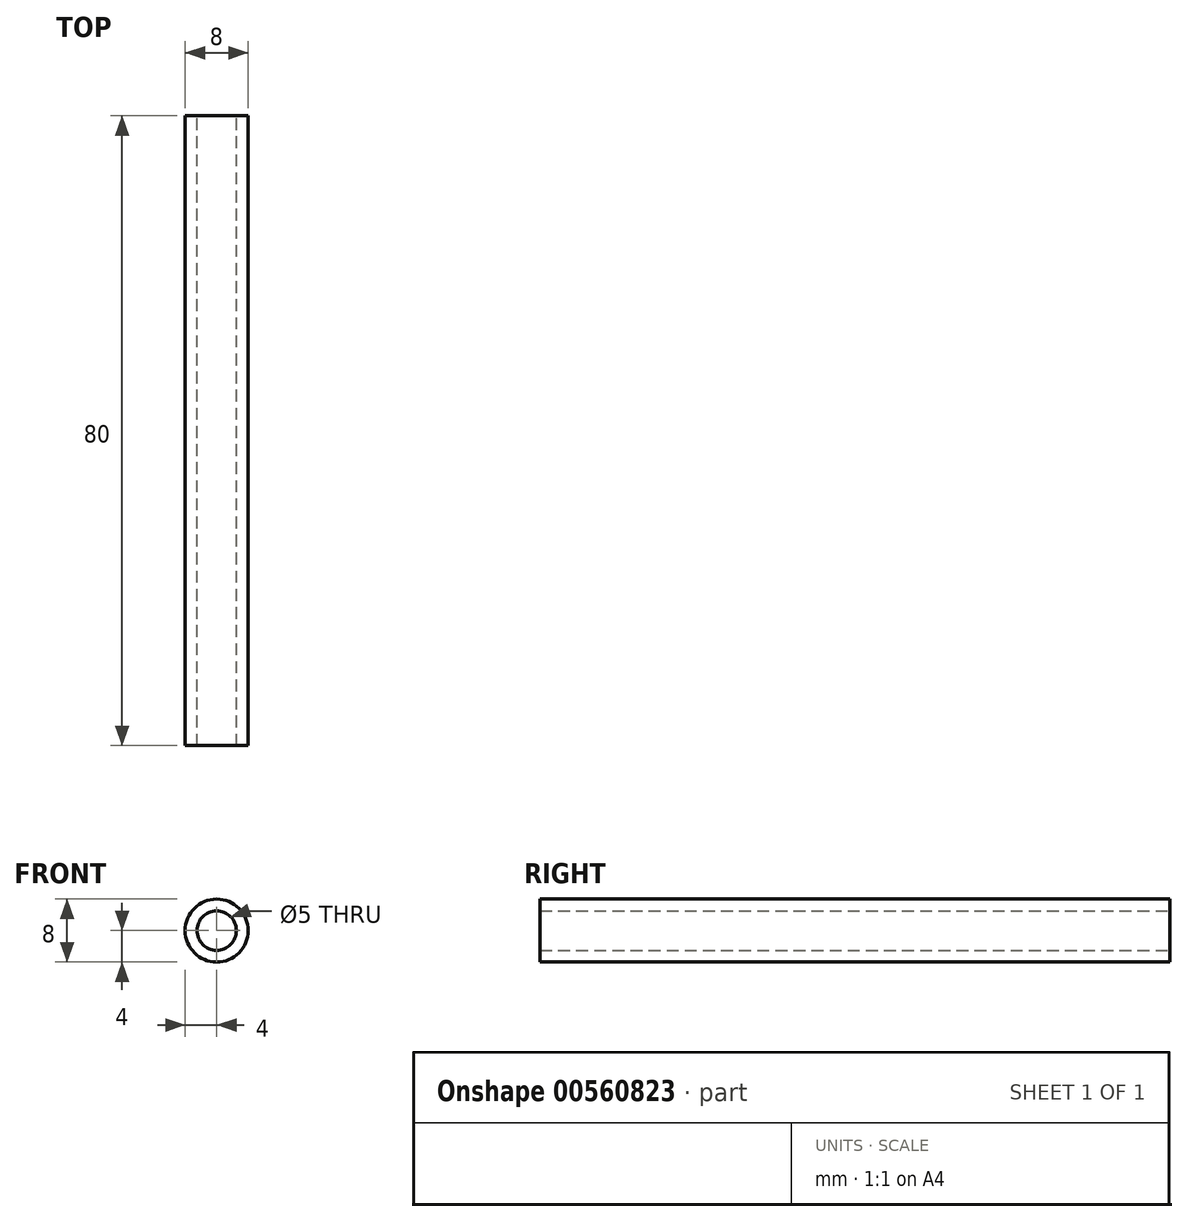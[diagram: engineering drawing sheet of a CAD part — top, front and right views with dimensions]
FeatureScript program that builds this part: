
annotation { "Feature Type Name" : "Feature", "Feature Type Description" : "" }
export const myFeature = defineFeature(function(context is Context, id is Id, definition is map)
    precondition{}
    {
        {
            var Q0;
            Q0=qCreatedBy(makeId("Front.planeOp"),FACE);
            var sketch = newSketch(context, id + "F0", { "sketchPlane" : qUnion([Q0])});
            skCircle(sketch, "E0", {"center": v(0, 0) * mm, "radius": 4 * mm});
            skCircle(sketch, "E1", {"center": v(0, 0) * mm, "radius": 2.5 * mm});
            skSolve(sketch);
        }
        {
            var Q0;
            Q0=qSketchRegion(id+"F0",true);
            extrude(context, id + "F1", {"entities" : qUnion([Q0]), "endBound" : BoundingType.SYMMETRIC, "depth" : 80 * mm, "offsetDistance" : 25 * mm});
        }
    });
